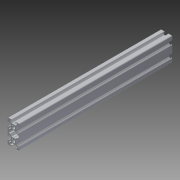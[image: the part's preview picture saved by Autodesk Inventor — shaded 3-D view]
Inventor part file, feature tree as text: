
AUTODESK INVENTOR PART (.ipt)
format: ipt  version: 2013 (Build 170138000, 138)  size: 481,280 bytes
history: native  units: in
note: dims shown in document units (in); Inventor stores cm internally (conversion verified against a paired STEP export)
features: other x3, extrude x1, sketch x1
ambient origin geometry x8: Origin, YZ Plane, XZ Plane, XY Plane, X Axis, Y Axis, Z Axis, Center Point
bodies: Solid1 (feature_tree)
feature tree (5):
  other  "Blocks"
  extrude  "Extrusion1"  [1 undecoded]
  sketch  "Sketch1"  dims[d1=0.0in]
  other  "Bosch 20x40 profile"
  other  "Bosch 20x40 profile:1"
note: 1 required parameter value undecoded (feature->parameter linkage not recoverable at this tier; creation-order binding heuristic only, values carry confidence <= 0.55)
